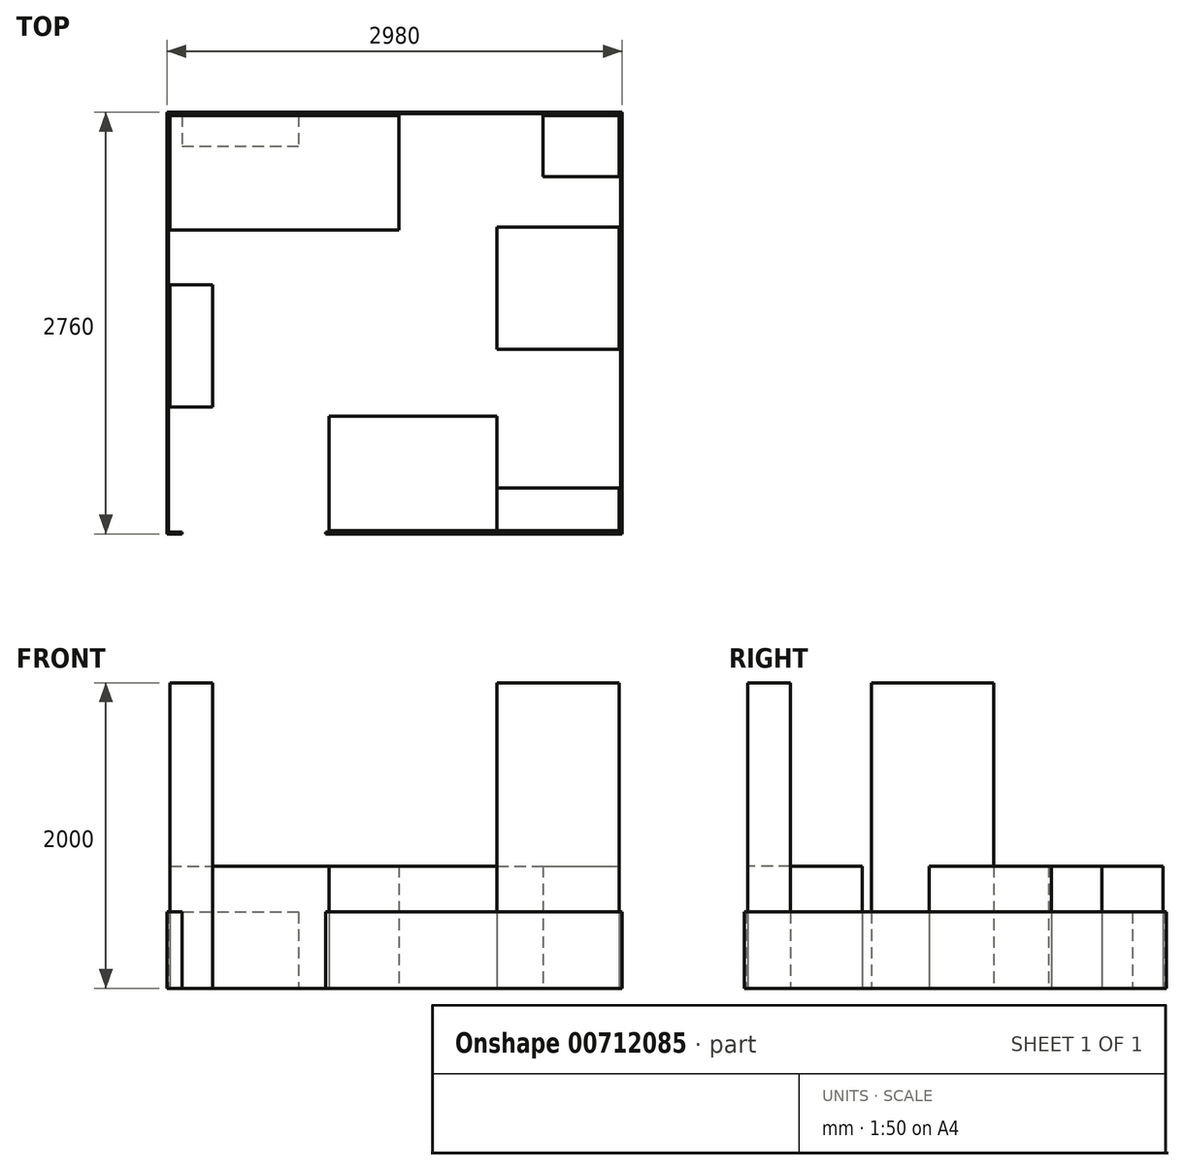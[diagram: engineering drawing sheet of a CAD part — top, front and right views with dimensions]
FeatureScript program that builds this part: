
annotation { "Feature Type Name" : "Feature", "Feature Type Description" : "" }
export const myFeature = defineFeature(function(context is Context, id is Id, definition is map)
    precondition{}
    {
        {
            var Q0;
            Q0=qCreatedBy(makeId("Top.planeOp"),FACE);
            var sketch = newSketch(context, id + "F0", { "sketchPlane" : qUnion([Q0])});
            skLineSegment(sketch, "E0.bottom", {"start": v(-1490, 1990) * mm, "end": v(1470, 1990) * mm});
            skLineSegment(sketch, "E0.top", {"start": v(-1490, -750) * mm, "end": v(-1400, -750) * mm});
            skLineSegment(sketch, "E0.left", {"start": v(-1490, 1990) * mm, "end": v(-1490, -750) * mm});
            skLineSegment(sketch, "E0.right", {"start": v(1470, 1990) * mm, "end": v(1470, -750) * mm});
            skLineSegment(sketch, "E1.0", {"start": v(-1500, 2000) * mm, "end": v(-1500, -760) * mm});
            skLineSegment(sketch, "E1.1", {"start": v(-1500, 2000) * mm, "end": v(1480, 2000) * mm});
            skLineSegment(sketch, "E1.2", {"start": v(1480, 2000) * mm, "end": v(1480, -760) * mm});
            skLineSegment(sketch, "E1.3", {"start": v(-1500, -760) * mm, "end": v(-1400, -760) * mm});
            skLineSegment(sketch, "E2", {"start": v(-1400, -750) * mm, "end": v(-1400, -760) * mm});
            skLineSegment(sketch, "E3", {"start": v(-460, -750) * mm, "end": v(-460, -760) * mm});
            skLineSegment(sketch, "E4.trimOffspring", {"start": v(-460, -750) * mm, "end": v(1470, -750) * mm});
            skLineSegment(sketch, "E5.trimOffspring", {"start": v(-460, -760) * mm, "end": v(1480, -760) * mm});
            skLineSegment(sketch, "E6.bottom", {"start": v(660, -460) * mm, "end": v(1460, -460) * mm});
            skLineSegment(sketch, "E6.top", {"start": v(660, -740) * mm, "end": v(1460, -740) * mm});
            skLineSegment(sketch, "E6.left", {"start": v(660, -460) * mm, "end": v(660, -740) * mm});
            skLineSegment(sketch, "E6.right", {"start": v(1460, -460) * mm, "end": v(1460, -740) * mm});
            skLineSegment(sketch, "E7.bottom", {"start": v(-1480, 70) * mm, "end": v(-1200, 70) * mm});
            skLineSegment(sketch, "E7.top", {"start": v(-1480, 870) * mm, "end": v(-1200, 870) * mm});
            skLineSegment(sketch, "E7.left", {"start": v(-1480, 70) * mm, "end": v(-1480, 870) * mm});
            skLineSegment(sketch, "E7.right", {"start": v(-1200, 70) * mm, "end": v(-1200, 870) * mm});
            skLineSegment(sketch, "E8.bottom", {"start": v(660, 1250) * mm, "end": v(1460, 1250) * mm});
            skLineSegment(sketch, "E8.top", {"start": v(660, 450) * mm, "end": v(1460, 450) * mm});
            skLineSegment(sketch, "E8.left", {"start": v(660, 1250) * mm, "end": v(660, 450) * mm});
            skLineSegment(sketch, "E8.right", {"start": v(1460, 1250) * mm, "end": v(1460, 450) * mm});
            skLineSegment(sketch, "E9.bottom", {"start": v(-440, -740) * mm, "end": v(660, -740) * mm});
            skLineSegment(sketch, "E9.top", {"start": v(-440, 10) * mm, "end": v(660, 10) * mm});
            skLineSegment(sketch, "E9.left", {"start": v(-440, -740) * mm, "end": v(-440, 10) * mm});
            skLineSegment(sketch, "E9.right", {"start": v(660, -740) * mm, "end": v(660, 10) * mm});
            skLineSegment(sketch, "E10.bottom", {"start": v(-1400, 1980) * mm, "end": v(-640, 1980) * mm});
            skLineSegment(sketch, "E10.top", {"start": v(-1400, 1780) * mm, "end": v(-640, 1780) * mm});
            skLineSegment(sketch, "E10.left", {"start": v(-1400, 1980) * mm, "end": v(-1400, 1780) * mm});
            skLineSegment(sketch, "E10.right", {"start": v(-640, 1980) * mm, "end": v(-640, 1780) * mm});
            skLineSegment(sketch, "E11.bottom", {"start": v(-1480, 1980) * mm, "end": v(20, 1980) * mm});
            skLineSegment(sketch, "E11.top", {"start": v(-1480, 1230) * mm, "end": v(20, 1230) * mm});
            skLineSegment(sketch, "E11.left", {"start": v(-1480, 1980) * mm, "end": v(-1480, 1230) * mm});
            skLineSegment(sketch, "E11.right", {"start": v(20, 1980) * mm, "end": v(20, 1230) * mm});
            skLineSegment(sketch, "E12.bottom", {"start": v(960, 1580) * mm, "end": v(1460, 1580) * mm});
            skLineSegment(sketch, "E12.top", {"start": v(960, 1980) * mm, "end": v(1460, 1980) * mm});
            skLineSegment(sketch, "E12.left", {"start": v(960, 1580) * mm, "end": v(960, 1980) * mm});
            skLineSegment(sketch, "E12.right", {"start": v(1460, 1580) * mm, "end": v(1460, 1980) * mm});
            skSolve(sketch);
        }
        {
            var Q0;
            Q0=makeQuery(id+"F0.imprint","IMPRINT",FACE,{"disambiguationData":[TD([[makeQuery(id+"F0.imprint","IMPRINT",EDGE,{"derivedFrom":sQuery(id+"F0.wireOp",EDGE,"E0.bottom")}),1.0]])]});
            extrude(context, id + "F1", {"entities" : qUnion([Q0]), "depth" : 500 * mm, "offsetDistance" : 25 * mm});
        }
        {
            var Q0;
            Q0=makeQuery(id+"F0.imprint","IMPRINT",FACE,{"disambiguationData":[TD([[makeQuery(id+"F0.imprint","IMPRINT",EDGE,{"derivedFrom":sQuery(id+"F0.wireOp",EDGE,"E7.bottom")}),1.0]])]});
            extrude(context, id + "F2", {"entities" : qUnion([Q0]), "depth" : 2000 * mm, "offsetDistance" : 25 * mm});
        }
        {
            var Q0;
            Q0=makeQuery(id+"F0.imprint","IMPRINT",FACE,{"disambiguationData":[TD([[makeQuery(id+"F0.imprint","IMPRINT",EDGE,{"derivedFrom":sQuery(id+"F0.wireOp",EDGE,"E10.top")}),1.0]])]});
            extrude(context, id + "F3", {"entities" : qUnion([Q0]), "depth" : 500 * mm, "offsetDistance" : 25 * mm});
        }
        {
            var Q0;
            Q0=makeQuery(id+"F0.imprint","IMPRINT",FACE,{"disambiguationData":[TD([[makeQuery(id+"F0.imprint","IMPRINT",EDGE,{"derivedFrom":sQuery(id+"F0.wireOp",EDGE,"E11.bottom")}),-1.0]])]});
            var Q1;
            {var subQ2=sQuery(id+"F0.wireOp",EDGE,"E10.left");Q1=makeQuery(id+"F0.imprint","IMPRINT",FACE,{"disambiguationData":[TD([[makeQuery(id+"F0.imprint","IMPRINT",EDGE,{"derivedFrom":subQ2}),-1.0]])]});}
            var Q2;
            Q2=makeQuery(id+"F0.imprint","IMPRINT",FACE,{"disambiguationData":[TD([[makeQuery(id+"F0.imprint","IMPRINT",EDGE,{"derivedFrom":sQuery(id+"F0.wireOp",EDGE,"E10.top")}),1.0]])]});
            extrude(context, id + "F4", {"entities" : qUnion([Q0, Q1, Q2]), "depth" : 800 * mm, "offsetDistance" : 25 * mm});
        }
        {
            var Q0;
            Q0=makeQuery(id+"F0.imprint","IMPRINT",FACE,{"disambiguationData":[TD([[makeQuery(id+"F0.imprint","IMPRINT",EDGE,{"derivedFrom":sQuery(id+"F0.wireOp",EDGE,"E9.bottom")}),1.0]])]});
            extrude(context, id + "F5", {"entities" : qUnion([Q0]), "depth" : 800 * mm, "offsetDistance" : 25 * mm});
        }
        {
            var Q0;
            Q0=makeQuery(id+"F0.imprint","IMPRINT",FACE,{"disambiguationData":[TD([[makeQuery(id+"F0.imprint","IMPRINT",EDGE,{"derivedFrom":sQuery(id+"F0.wireOp",EDGE,"E6.bottom")}),-1.0]])]});
            extrude(context, id + "F6", {"entities" : qUnion([Q0]), "depth" : 2000 * mm, "offsetDistance" : 25 * mm});
        }
        {
            var Q0;
            Q0=makeQuery(id+"F0.imprint","IMPRINT",FACE,{"disambiguationData":[TD([[makeQuery(id+"F0.imprint","IMPRINT",EDGE,{"derivedFrom":sQuery(id+"F0.wireOp",EDGE,"E8.bottom")}),-1.0]])]});
            extrude(context, id + "F7", {"entities" : qUnion([Q0]), "depth" : 800 * mm, "offsetDistance" : 25 * mm});
        }
        {
            var Q0;
            Q0=makeQuery(id+"F0.imprint","IMPRINT",FACE,{"disambiguationData":[TD([[makeQuery(id+"F0.imprint","IMPRINT",EDGE,{"derivedFrom":sQuery(id+"F0.wireOp",EDGE,"E12.bottom")}),1.0]])]});
            extrude(context, id + "F8", {"entities" : qUnion([Q0]), "depth" : 800 * mm, "offsetDistance" : 25 * mm});
        }
    });
